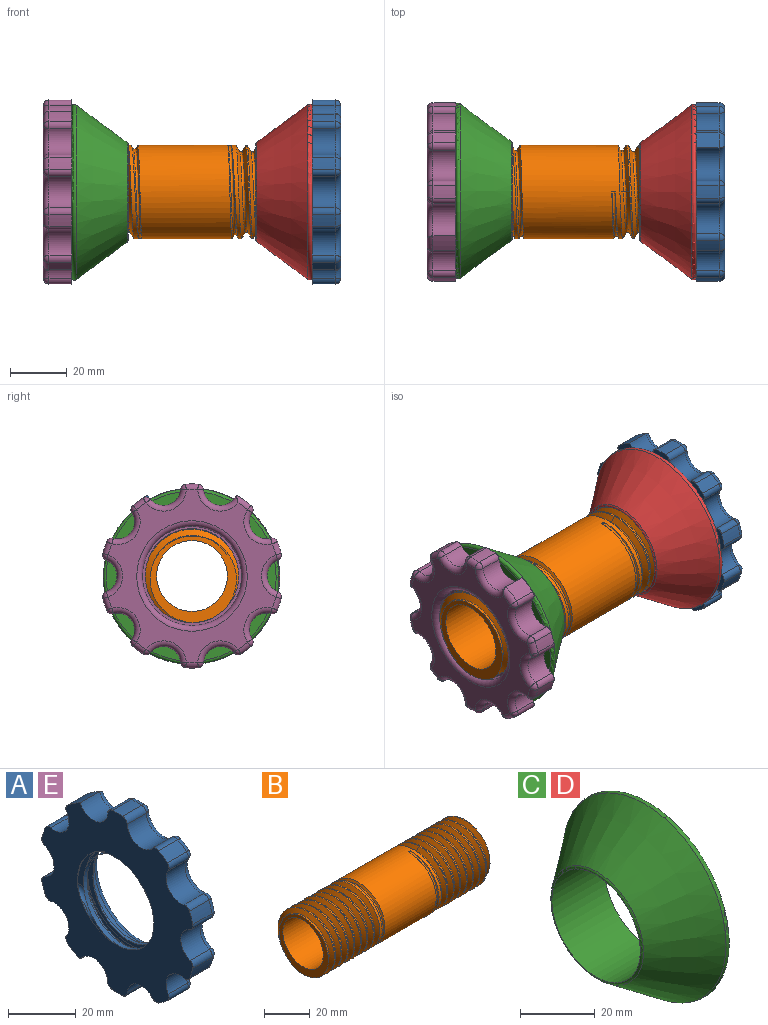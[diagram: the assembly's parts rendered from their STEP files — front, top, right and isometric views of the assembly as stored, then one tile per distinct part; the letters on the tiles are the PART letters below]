
ASSEMBLY  parts=5 mates=2
PART A: 85 faces, bbox 10x63.2x65.1 mm
  f0: plane 35x35mm, normal (1,0,0), area 176.7mm2, adj f10,f12,f43
  f1: cylinder r=32.5mm len=8mm, axis (1,0,0), area 35.1mm2, adj f11,f24,f27,f76
  f2: cylinder r=32.5mm len=8mm, axis (1,0,0), area 35.1mm2, adj f11,f26,f29,f84
  f3: cylinder r=32.5mm len=8mm, axis (1,0,0), area 35.1mm2, adj f11,f28,f31,f77
  f4: cylinder r=32.5mm len=8mm, axis (1,0,0), area 35.1mm2, adj f11,f30,f33,f69
  f5: cylinder r=32.5mm len=8mm, axis (1,0,0), area 35.1mm2, adj f11,f32,f35,f61
  f6: cylinder r=32.5mm len=8mm, axis (1,0,0), area 51.2mm2, adj f11,f17,f34,f53
  f7: cylinder r=32.5mm len=8mm, axis (1,0,0), area 35.1mm2, adj f11,f36,f38,f47
  f8: cylinder r=32.5mm len=8mm, axis (1,0,0), area 35.1mm2, adj f11,f37,f40,f52
  f9: cylinder r=32.5mm len=8mm, axis (1,0,0), area 35.1mm2, adj f11,f39,f42,f60
  f10: cylinder r=15.2mm len=30.4mm, axis (1,0,0), area 183.4mm2, adj f0,f11
  f11: plane 65x63.15mm, normal (-1,0,0), area 1975.6mm2, adj f1,f2,f3,f4,f5,f6,f7,f8
  f12: cylinder r=16.7mm len=33.4mm, axis (-1,0,0), area 96.2mm2, adj f0,f11
  f13: cylinder r=32.5mm len=8mm, axis (1,0,0), area 35.1mm2, adj f11,f25,f41,f68
  f14: cylinder r=6mm len=11.17mm, axis (1,0,0), area 114.9mm2, adj f11,f41,f42,f64
  f15: cylinder r=6mm len=9.23mm, axis (1,0,0), area 114.9mm2, adj f11,f39,f40,f56
  f16: cylinder r=6mm len=10.62mm, axis (1,0,0), area 114.9mm2, adj f11,f37,f38,f48
  f17: cylinder r=6mm len=11.5mm, axis (1,0,0), area 128.4mm2, adj f6,f11,f36,f51
  f18: cylinder r=6mm len=9.23mm, axis (1,0,0), area 114.9mm2, adj f11,f34,f35,f57
  f19: cylinder r=6mm len=11.17mm, axis (1,0,0), area 114.9mm2, adj f11,f32,f33,f65
  f20: cylinder r=6mm len=9.23mm, axis (1,0,0), area 114.9mm2, adj f11,f30,f31,f73
  f21: cylinder r=6mm len=10.62mm, axis (1,0,0), area 114.9mm2, adj f11,f28,f29,f81
  f22: cylinder r=6mm len=10.62mm, axis (1,0,0), area 114.9mm2, adj f11,f26,f27,f80
  f23: cylinder r=6mm len=9.23mm, axis (1,0,0), area 114.9mm2, adj f11,f24,f25,f72
  f24: cylinder r=2mm len=8mm, axis (-1,0,0), area 23.1mm2, adj f1,f11,f23,f74
  f25: cylinder r=2mm len=8mm, axis (1,0,0), area 23.1mm2, adj f11,f13,f23,f70
  f26: cylinder r=2mm len=8mm, axis (-1,0,0), area 23.1mm2, adj f2,f11,f22,f82
  f27: cylinder r=2mm len=8mm, axis (1,0,0), area 23.1mm2, adj f1,f11,f22,f78
  f28: cylinder r=2mm len=8mm, axis (-1,0,0), area 23.1mm2, adj f3,f11,f21,f79
  f29: cylinder r=2mm len=8mm, axis (1,0,0), area 23.1mm2, adj f2,f11,f21,f83
  f30: cylinder r=2mm len=8mm, axis (-1,0,0), area 23.1mm2, adj f4,f11,f20,f71
  f31: cylinder r=2mm len=8mm, axis (1,0,0), area 23.1mm2, adj f3,f11,f20,f75
  f32: cylinder r=2mm len=8mm, axis (-1,0,0), area 23.1mm2, adj f5,f11,f19,f63
  f33: cylinder r=2mm len=8mm, axis (1,0,0), area 23.1mm2, adj f4,f11,f19,f67
  f34: cylinder r=2mm len=8mm, axis (-1,0,0), area 23.1mm2, adj f6,f11,f18,f55
  f35: cylinder r=2mm len=8mm, axis (1,0,0), area 23.1mm2, adj f5,f11,f18,f59
  f36: cylinder r=2mm len=8mm, axis (-1,0,0), area 23.1mm2, adj f7,f11,f17,f49
  f37: cylinder r=2mm len=8mm, axis (-1,0,0), area 23.1mm2, adj f8,f11,f16,f50
  f38: cylinder r=2mm len=8mm, axis (1,0,0), area 23.1mm2, adj f7,f11,f16,f46
  f39: cylinder r=2mm len=8mm, axis (-1,0,0), area 23.1mm2, adj f9,f11,f15,f58
  f40: cylinder r=2mm len=8mm, axis (1,0,0), area 23.1mm2, adj f8,f11,f15,f54
  f41: cylinder r=2mm len=8mm, axis (-1,0,0), area 23.1mm2, adj f11,f13,f14,f66
  f42: cylinder r=2mm len=8mm, axis (1,0,0), area 23.1mm2, adj f9,f11,f14,f62
  f43: cylinder r=17.5mm len=35mm, axis (-1,0,0), area 329.9mm2, adj f0,f45
  f44: plane 61x59.15mm, normal (1,0,0), area 1087.7mm2, adj f45,f47,f48,f51,f52,f53,f56,f57
  f45: torus R=19.5mm, axis (1,0,0), area 359.8mm2, adj f43,f44
  f46: sphere r=2mm, area 3.6mm2, adj f38,f47,f48
  f47: torus R=30.5mm, axis (1,0,0), area 13.5mm2, adj f7,f44,f46,f49
  f48: torus R=8mm, axis (1,0,0), area 50.6mm2, adj f16,f44,f46,f50
  f49: sphere r=2mm, area 8.1mm2, adj f36,f47,f51
  f50: sphere r=2mm, area 5.8mm2, adj f37,f48,f52
  f51: torus R=8mm, axis (1,0,0), area 53.4mm2, adj f17,f44,f49,f53
  f52: torus R=30.5mm, axis (1,0,0), area 13.5mm2, adj f8,f44,f50,f54
  f53: torus R=30.5mm, axis (1,0,0), area 16.6mm2, adj f6,f44,f51,f55
  f54: sphere r=2mm, area 5.8mm2, adj f40,f52,f56
  f55: sphere r=2mm, area 7.2mm2, adj f34,f53,f57
  f56: torus R=8mm, axis (1,0,0), area 50.6mm2, adj f15,f44,f54,f58
  f57: torus R=8mm, axis (1,0,0), area 50.6mm2, adj f18,f44,f55,f59
  f58: sphere r=2mm, area 5.8mm2, adj f39,f56,f60
  f59: sphere r=2mm, area 5.8mm2, adj f35,f57,f61
  f60: torus R=30.5mm, axis (1,0,0), area 13.5mm2, adj f9,f44,f58,f62
  f61: torus R=30.5mm, axis (1,0,0), area 13.5mm2, adj f5,f44,f59,f63
  f62: sphere r=2mm, area 5.8mm2, adj f42,f60,f64
  f63: sphere r=2mm, area 3.7mm2, adj f32,f61,f65
  f64: torus R=8mm, axis (1,0,0), area 50.6mm2, adj f14,f44,f62,f66
  f65: torus R=8mm, axis (1,0,0), area 50.6mm2, adj f19,f44,f63,f67
  f66: sphere r=2mm, area 5.8mm2, adj f41,f64,f68
  f67: sphere r=2mm, area 7.7mm2, adj f33,f65,f69
  f68: torus R=30.5mm, axis (1,0,0), area 13.5mm2, adj f13,f44,f66,f70
  f69: torus R=30.5mm, axis (1,0,0), area 13.5mm2, adj f4,f44,f67,f71
  f70: sphere r=2mm, area 5.8mm2, adj f25,f68,f72
  f71: sphere r=2mm, area 4mm2, adj f30,f69,f73
  f72: torus R=8mm, axis (1,0,0), area 50.6mm2, adj f23,f44,f70,f74
  f73: torus R=8mm, axis (1,0,0), area 50.6mm2, adj f20,f44,f71,f75
  f74: sphere r=2mm, area 5.8mm2, adj f24,f72,f76
  f75: sphere r=2mm, area 6.8mm2, adj f31,f73,f77
  f76: torus R=30.5mm, axis (1,0,0), area 13.5mm2, adj f1,f44,f74,f78
  f77: torus R=30.5mm, axis (1,0,0), area 13.5mm2, adj f3,f44,f75,f79
  f78: sphere r=2mm, area 4.5mm2, adj f27,f76,f80
  f79: sphere r=2mm, area 5.8mm2, adj f28,f77,f81
  f80: torus R=8mm, axis (1,0,0), area 50.6mm2, adj f22,f44,f78,f82
  f81: torus R=8mm, axis (1,0,0), area 50.6mm2, adj f21,f44,f79,f83
  f82: sphere r=2mm, area 5.8mm2, adj f26,f80,f84
  f83: sphere r=2mm, area 3.7mm2, adj f29,f81,f84
  f84: torus R=30.5mm, axis (1,0,0), area 13.5mm2, adj f2,f44,f82,f83
PART B: 34 faces, bbox 104.3x39.2x38.1 mm
  f0: cylinder r=16.5mm len=42mm, axis (1,0,0), area 3619.7mm2, adj f1,f9,f21,f22,f23,f25,f27,f28
  f1: cylinder r=16.5mm len=33mm, axis (1,0,0), area 52mm2, adj f0,f2,f20,f21
  f2: cylinder r=16.5mm len=33mm, axis (1,0,0), area 51.8mm2, adj f1,f3,f20,f21
  f3: cylinder r=16.5mm len=33mm, axis (1,0,0), area 51.7mm2, adj f2,f4,f20,f21
  f4: cylinder r=16.5mm len=33mm, axis (1,0,0), area 51.9mm2, adj f3,f5,f20,f21
  f5: cylinder r=16.5mm len=33mm, axis (1,0,0), area 51.9mm2, adj f4,f6,f20,f21
  f6: cylinder r=16.5mm len=33mm, axis (1,0,0), area 51.9mm2, adj f5,f7,f20,f21
  f7: cylinder r=16.5mm len=33mm, axis (1,0,0), area 51.6mm2, adj f6,f8,f20,f21
  f8: cylinder r=16.5mm len=11.56mm, axis (1,0,0), area 3.2mm2, adj f7,f18,f20
  f9: cylinder r=16.5mm len=33mm, axis (1,0,0), area 66.6mm2, adj f0,f10,f28,f31,f32
  f10: cylinder r=16.5mm len=33mm, axis (1,0,0), area 52mm2, adj f9,f11,f31,f32
  f11: cylinder r=16.5mm len=33mm, axis (1,0,0), area 51.8mm2, adj f10,f12,f31,f32
  f12: cylinder r=16.5mm len=33mm, axis (1,0,0), area 51.9mm2, adj f11,f13,f31,f32
  f13: cylinder r=16.5mm len=33mm, axis (1,0,0), area 51.7mm2, adj f12,f14,f31,f32
  f14: cylinder r=16.5mm len=33mm, axis (1,0,0), area 52mm2, adj f13,f15,f31,f32
  f15: cylinder r=16.5mm len=33mm, axis (1,0,0), area 51.9mm2, adj f14,f16,f31,f32
  f16: cylinder r=16.5mm len=33mm, axis (1,0,0), area 29mm2, adj f15,f26,f31,f32
  f17: cylinder r=12.5mm len=100mm, axis (1,0,0), area 7854mm2, adj f18,f26
  f18: plane 31.81x31.63mm, normal (-1,0,0), area 241.6mm2, adj f8,f17,f19,f20,f21
  f19: bspline ~33.11x32.33mm, area 756.4mm2, adj f18,f20,f21,f24
  f20: bspline ~32.97x32.97mm, area 1763.1mm2, adj f1,f2,f3,f4,f5,f6,f7,f8
  f21: bspline ~38.11x33.25mm, area 1897.9mm2, adj f0,f1,f2,f3,f4,f5,f6,f7
  f22: plane 1.22x0.41mm, normal (0,-1,0), area 0.3mm2, adj f0,f23,f24,f25
  f23: bspline ~36.13x35.26mm, area 133.5mm2, adj f0,f20,f22,f24
  f24: bspline ~31.78x30.9mm, area 107mm2, adj f19,f22,f23,f25
  f25: bspline ~36.13x35.26mm, area 133.4mm2, adj f0,f21,f22,f24
  f26: plane 31.81x31.63mm, normal (1,0,0), area 241.6mm2, adj f16,f17,f30,f31,f32
  f27: plane 1.22x0.41mm, normal (0,-1,0), area 0.3mm2, adj f0,f28,f29,f33
  f28: bspline ~36.13x35.26mm, area 133.5mm2, adj f0,f9,f27,f31,f33
  f29: bspline ~36.13x35.26mm, area 133.4mm2, adj f0,f27,f32,f33
  f30: bspline ~33.11x32.33mm, area 756.4mm2, adj f26,f31,f32,f33
  f31: bspline ~32.97x32.97mm, area 1763.2mm2, adj f9,f10,f11,f12,f13,f14,f15,f16
  f32: bspline ~38.11x33.25mm, area 1897.9mm2, adj f0,f9,f10,f11,f12,f13,f14,f15
  f33: bspline ~31.78x30.9mm, area 107mm2, adj f27,f28,f29,f30
PART C: 5 faces, bbox 20x67.2x67.2 mm
  f0: cylinder r=16.75mm len=33.5mm, axis (-1,0,0), area 2104.9mm2, adj f2,f3
  f1: cone r=17.25mm half-angle=36.4deg, axis (1,0,0), area 3399mm2, adj f3,f4
  f2: plane 60.04x60.04mm, normal (1,0,0), area 1949.8mm2, adj f0,f4
  f3: torus R=16.74mm, axis (-1,0,0), area 100.4mm2, adj f0,f1
  f4: torus R=30.02mm, axis (-1,0,0), area 426.2mm2, adj f1,f2
PART D: same geometry as C
PART E: same geometry as A
PLACE A at identity
PLACE B at identity
PLACE C rot(axis=(0,0,-1),180deg) t=(5,0.31,-0.12)mm
PLACE D at identity
PLACE E rot(axis=(0,0,1),180deg) t=(5,0,0)mm
MATE fastened E.f43 <-> B.f17  axis (-1,0,0) through (-50,0,0)mm
MATE fastened C.f0 <-> E.f11  axis (-1,0,0) through (-40,0.31,-0.12)mm
